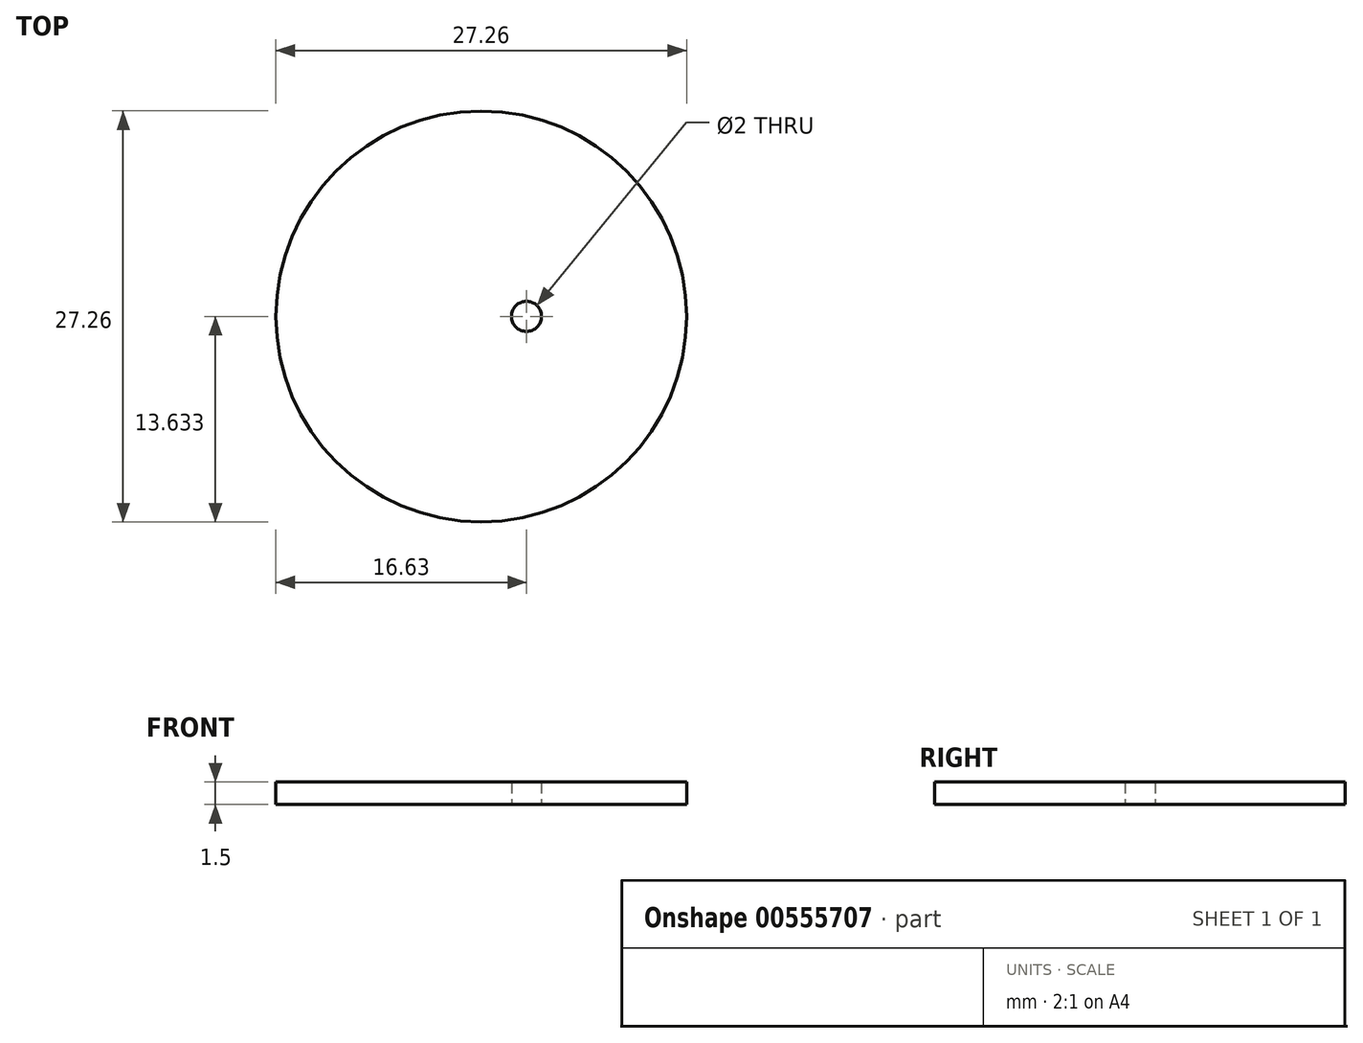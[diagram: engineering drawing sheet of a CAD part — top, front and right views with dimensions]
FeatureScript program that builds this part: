
annotation { "Feature Type Name" : "Feature", "Feature Type Description" : "" }
export const myFeature = defineFeature(function(context is Context, id is Id, definition is map)
    precondition{}
    {
        {
            var Q0;
            Q0=qCreatedBy(makeId("Top.planeOp"),FACE);
            var sketch = newSketch(context, id + "F0", { "sketchPlane" : qUnion([Q0])});
            skCircle(sketch, "E0", {"center": v(0, 0) * mm, "radius": 13.62 * mm});
            skCircle(sketch, "E1", {"center": v(3, 0) * mm, "radius": 1 * mm});
            skSolve(sketch);
        }
        {
            var Q0;
            Q0 = qSketchRegion(id + "F0", true);
            extrude(context, id + "F1", {"entities" : qUnion([Q0]), "depth" : 1.5 * mm, "offsetDistance" : 25.4 * mm});
        }
    });
